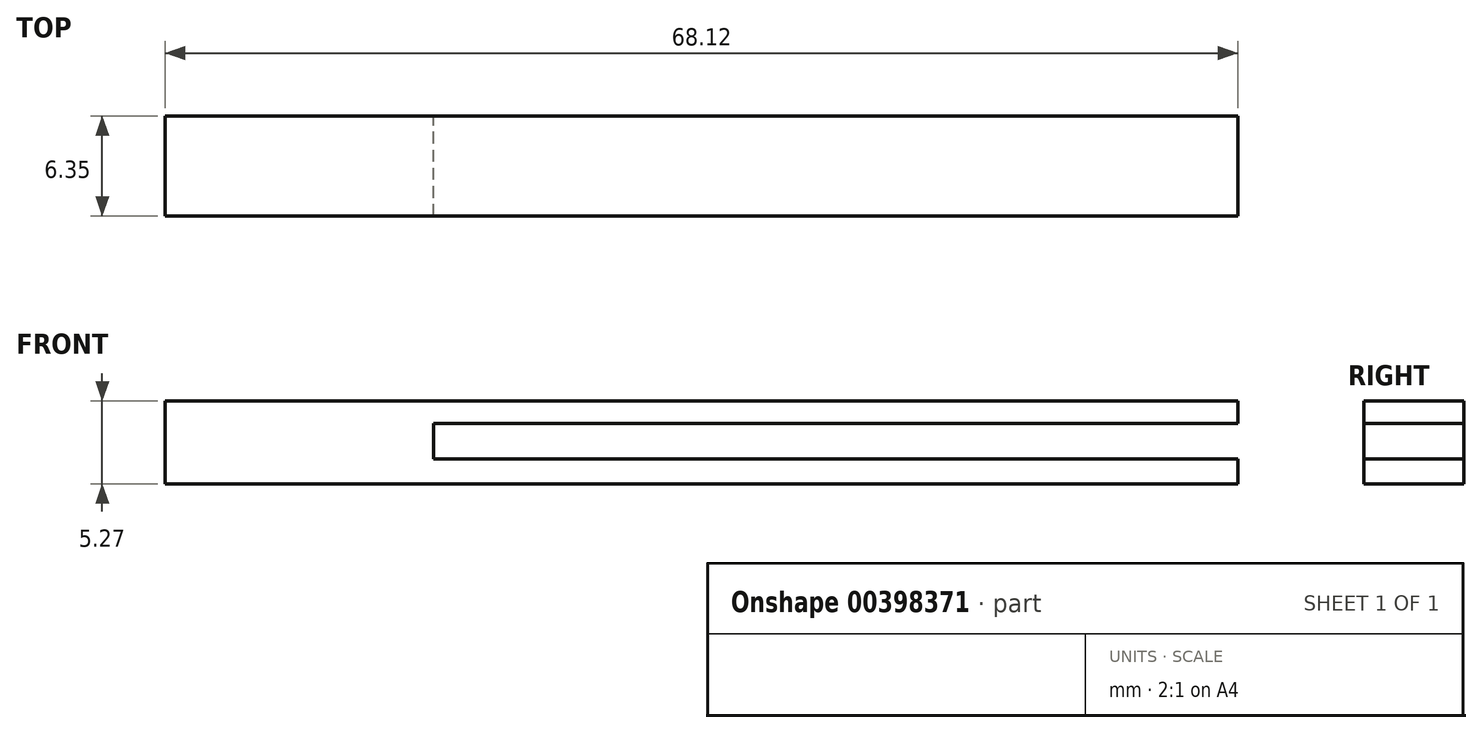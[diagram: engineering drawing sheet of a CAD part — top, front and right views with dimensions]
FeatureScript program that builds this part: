
annotation { "Feature Type Name" : "Feature", "Feature Type Description" : "" }
export const myFeature = defineFeature(function(context is Context, id is Id, definition is map)
    precondition{}
    {
        {
            var Q0;
            Q0=qCreatedBy(makeId("Front.planeOp"),FACE);
            var sketch = newSketch(context, id + "F0", { "sketchPlane" : qUnion([Q0])});
            skLineSegment(sketch, "E0.bottom", {"start": v(0, 0) * mm, "end": v(68.12, 0) * mm});
            skLineSegment(sketch, "E0.top", {"start": v(0, -5.27) * mm, "end": v(68.12, -5.27) * mm});
            skLineSegment(sketch, "E0.left", {"start": v(0, 0) * mm, "end": v(0, -5.27) * mm});
            skLineSegment(sketch, "E0.right", {"start": v(68.12, 0) * mm, "end": v(68.12, -5.27) * mm});
            skSolve(sketch);
        }
        {
            var Q0;
            Q0 = qSketchRegion(id + "F0", true);
            extrude(context, id + "F1", {"entities" : qUnion([Q0]), "depth" : 6.35 * mm});
        }
        {
            var Q0;
            Q0=makeQuery(id+"F1.opExtrude","CAP_FACE",FACE,{"disambiguationData":[OSD([sQuery(id+"F0.wireOp",EDGE,"E0.bottom"),sQuery(id+"F0.wireOp",EDGE,"E0.top"),sQuery(id+"F0.wireOp",EDGE,"E0.left"),sQuery(id+"F0.wireOp",EDGE,"E0.right")])],"isStart":true});
            var sketch = newSketch(context, id + "F2", { "sketchPlane" : qUnion([Q0])});
            skSolve(sketch);
        }
        {
            var Q0;
            Q0=makeQuery(id+"F2.imprint","IMPRINT",FACE,{"disambiguationData":[TD([[makeQuery(id+"F2.imprint","IMPRINT",EDGE,{"derivedFrom":makeQuery(id+"F1.opExtrude","CAP_EDGE",EDGE,{"disambiguationData":[OSD([sQuery(id+"F0.wireOp",EDGE,"E0.bottom")])],"isStart":true})}),1.0]])]});
            var sketch = newSketch(context, id + "F3", { "sketchPlane" : qUnion([Q0])});
            skLineSegment(sketch, "E1.bottom", {"start": v(-68.16, -1.43) * mm, "end": v(-17.05, -1.43) * mm});
            skLineSegment(sketch, "E1.top", {"start": v(-68.16, -3.67) * mm, "end": v(-17.05, -3.67) * mm});
            skLineSegment(sketch, "E1.left", {"start": v(-68.16, -1.43) * mm, "end": v(-68.16, -3.67) * mm});
            skLineSegment(sketch, "E1.right", {"start": v(-17.05, -1.43) * mm, "end": v(-17.05, -3.67) * mm});
            skSolve(sketch);
        }
        {
            var Q0;
            Q0 = qSketchRegion(id + "F3", true);
            extrude(context, id + "F4", {"entities" : qUnion([Q0]), "operationType" : NewBodyOperationType.REMOVE, "oppositeDirection" : true, "depth" : 6.35 * mm});
        }
    });
